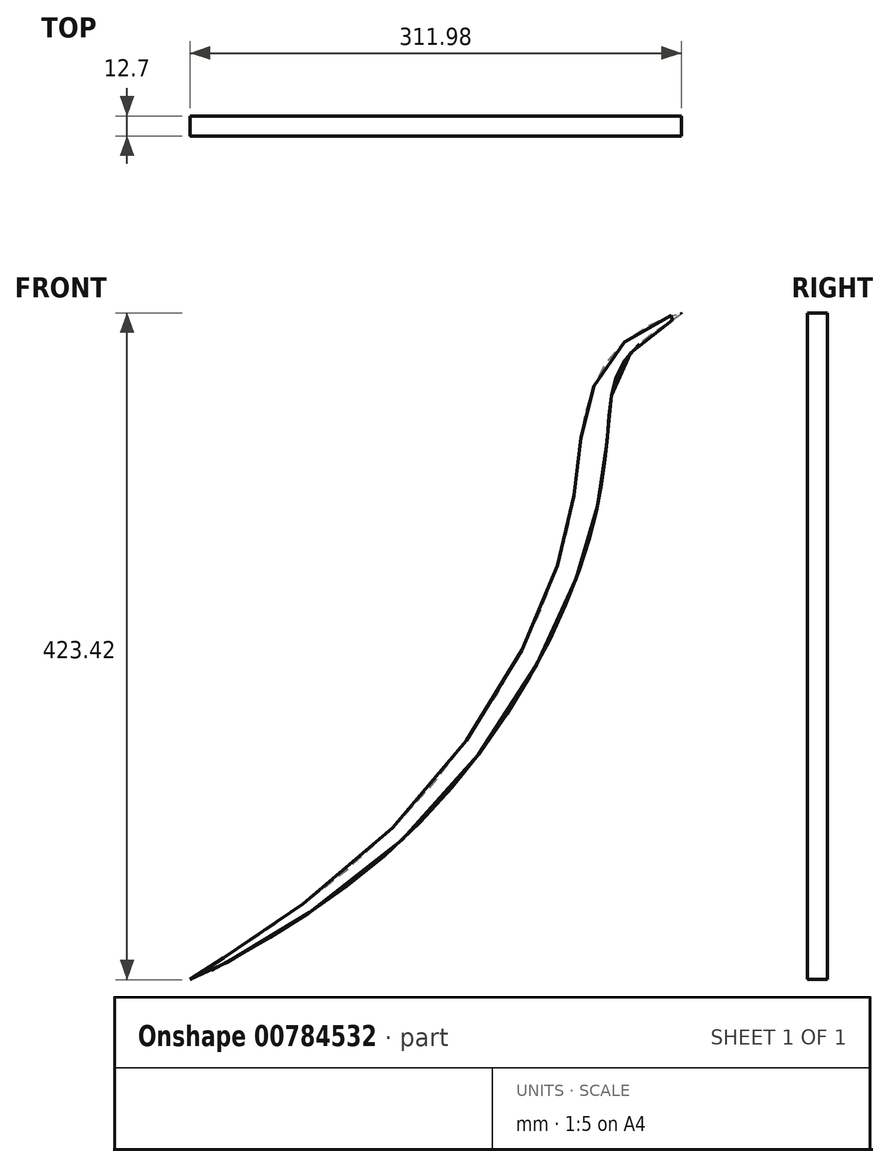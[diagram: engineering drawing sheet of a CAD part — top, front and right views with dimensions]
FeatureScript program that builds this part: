
annotation { "Feature Type Name" : "Feature", "Feature Type Description" : "" }
export const myFeature = defineFeature(function(context is Context, id is Id, definition is map)
    precondition{}
    {
        {
            var Q0;
            Q0=qCreatedBy(makeId("Front.planeOp"),FACE);
            var sketch = newSketch(context, id + "F0", { "sketchPlane" : qUnion([Q0])});
            skFitSpline(sketch, "E0", {"points": [v(-250.09, -203.08) * mm, v(-134.55, -119.31) * mm, v(-13.23, 71.33) * mm, v(0, 152.21) * mm, v(28.66, 204.2) * mm, v(61.88, 220.1) * mm, v(30.1, 195.54) * mm, v(15.66, 150.77) * mm, v(0, 65.56) * mm, v(-127.32, -125.09) * mm, v(-250.09, -203.08) * mm]});
            skSolve(sketch);
        }
        {
            var Q0;
            Q0 = qSketchRegion(id + "F0", true);
            extrude(context, id + "F1", {"entities" : qUnion([Q0]), "depth" : 12.7 * mm, "offsetDistance" : 25.4 * mm});
        }
    });
